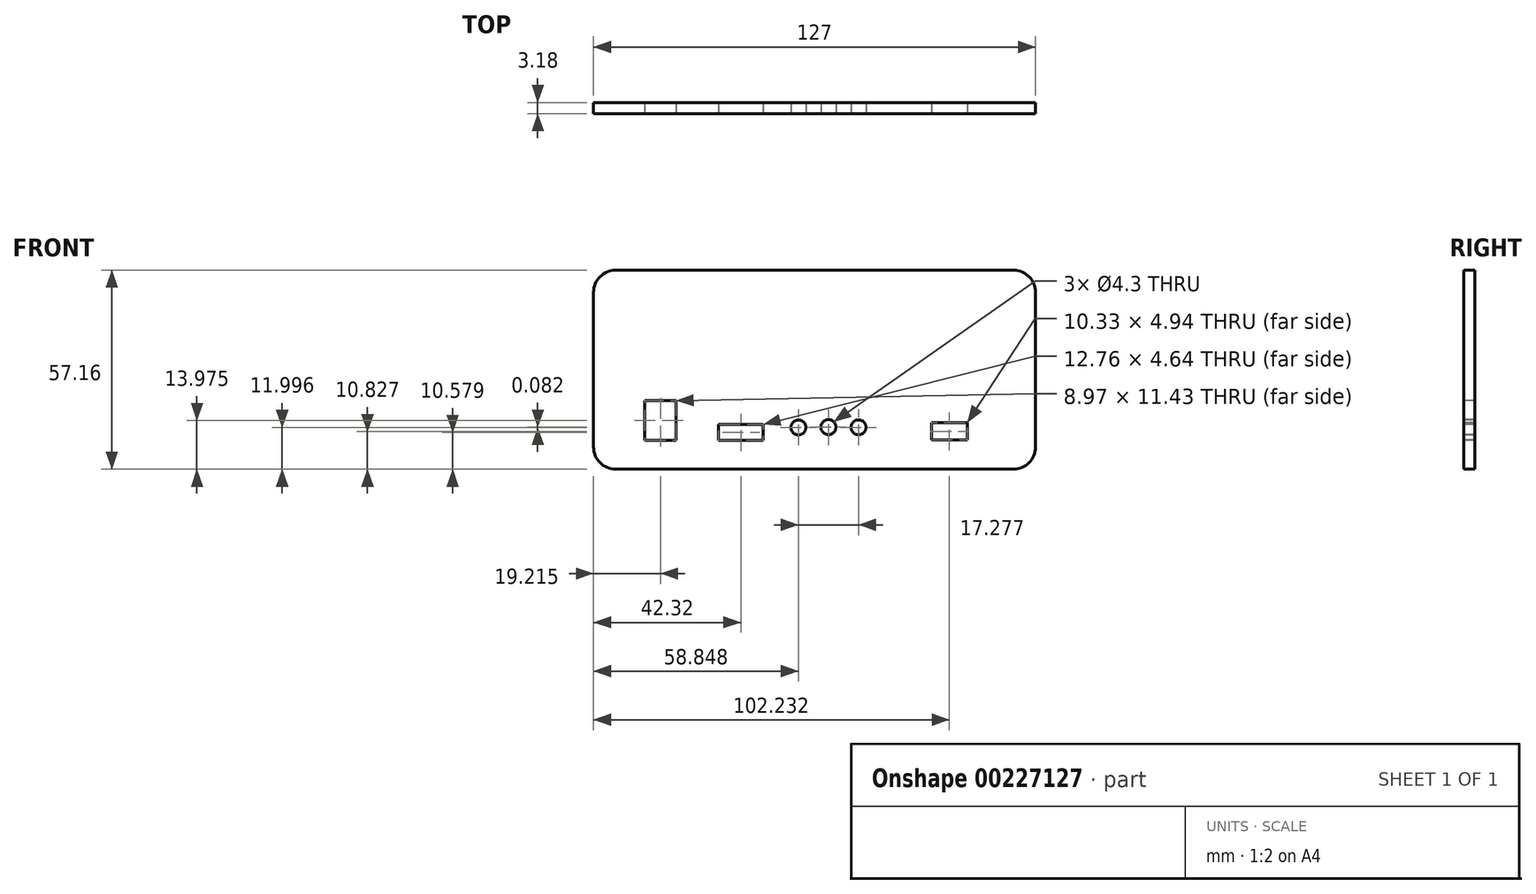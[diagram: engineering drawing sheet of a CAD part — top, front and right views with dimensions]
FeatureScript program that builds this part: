
annotation { "Feature Type Name" : "Feature", "Feature Type Description" : "" }
export const myFeature = defineFeature(function(context is Context, id is Id, definition is map)
    precondition{}
    {
        {
            var Q0;
            Q0=qCreatedBy(makeId("Front.planeOp"),FACE);
            var sketch = newSketch(context, id + "F0", { "sketchPlane" : qUnion([Q0])});
            skLineSegment(sketch, "E0.bottom", {"start": v(57.15, 28.58) * mm, "end": v(-57.15, 28.58) * mm});
            skLineSegment(sketch, "E0.top", {"start": v(57.15, -28.58) * mm, "end": v(-57.15, -28.58) * mm});
            skLineSegment(sketch, "E0.left", {"start": v(63.5, 22.22) * mm, "end": v(63.5, -22.22) * mm});
            skLineSegment(sketch, "E0.right", {"start": v(-63.5, 22.22) * mm, "end": v(-63.5, -22.22) * mm});
            skPoint(sketch, "E0.middle", {"position": v(0, 0) * mm});
            skPoint(sketch, "E1.visualSharp", {"position": v(-63.5, 28.58) * mm});
            skArc(sketch, "E1.filletArc", {"start": v(-57.15, 28.58) * mm, "mid": v(-61.64, 26.72) * mm, "end": v(-63.5, 22.22) * mm});
            skPoint(sketch, "E2.visualSharp", {"position": v(-63.5, -28.58) * mm});
            skArc(sketch, "E2.filletArc", {"start": v(-63.5, -22.22) * mm, "mid": v(-61.64, -26.72) * mm, "end": v(-57.15, -28.57) * mm});
            skPoint(sketch, "E3.visualSharp", {"position": v(63.5, -28.58) * mm});
            skArc(sketch, "E3.filletArc", {"start": v(57.15, -28.58) * mm, "mid": v(61.64, -26.72) * mm, "end": v(63.5, -22.22) * mm});
            skPoint(sketch, "E4.visualSharp", {"position": v(63.5, 28.58) * mm});
            skArc(sketch, "E4.filletArc", {"start": v(63.5, 22.22) * mm, "mid": v(61.64, 26.72) * mm, "end": v(57.15, 28.58) * mm});
            skSolve(sketch);
        }
        {
            var Q0;
            Q0=makeQuery(id+"F0.imprint","IMPRINT",FACE,{"disambiguationData":[TD([[makeQuery(id+"F0.imprint","IMPRINT",EDGE,{"derivedFrom":sQuery(id+"F0.wireOp",EDGE,"E0.bottom")}),1.0]])]});
            extrude(context, id + "F1", {"entities" : qUnion([Q0]), "depth" : 3.17 * mm, "offsetDistance" : 25.4 * mm});
        }
        {
            var Q0;
            Q0=makeQuery(id+"F1.opExtrude","CAP_FACE",FACE,{"disambiguationData":[OSD([sQuery(id+"F0.wireOp",EDGE,"E0.bottom"),sQuery(id+"F0.wireOp",EDGE,"E0.top"),sQuery(id+"F0.wireOp",EDGE,"E0.left"),sQuery(id+"F0.wireOp",EDGE,"E0.right")])],"isStart":false});
            var sketch = newSketch(context, id + "F2", { "sketchPlane" : qUnion([Q0])});
            skLineSegment(sketch, "E5.bottom", {"start": v(-60.32, 25.4) * mm, "end": v(60.33, 25.4) * mm, "construction": true});
            skLineSegment(sketch, "E5.top", {"start": v(-60.33, -25.4) * mm, "end": v(60.32, -25.4) * mm, "construction": true});
            skLineSegment(sketch, "E5.left", {"start": v(-60.32, 25.4) * mm, "end": v(-60.33, -25.4) * mm, "construction": true});
            skLineSegment(sketch, "E5.right", {"start": v(60.33, 25.4) * mm, "end": v(60.32, -25.4) * mm, "construction": true});
            skLineSegment(sketch, "E6", {"start": v(-60.33, -25.4) * mm, "end": v(-57.15, -25.4) * mm, "construction": true});
            skLineSegment(sketch, "E7", {"start": v(-57.15, -25.4) * mm, "end": v(-48.77, -25.4) * mm, "construction": true});
            skLineSegment(sketch, "E8", {"start": v(0, -25.4) * mm, "end": v(0, -20.32) * mm, "construction": true});
            skLineSegment(sketch, "E9", {"start": v(0, -20.32) * mm, "end": v(-60.33, -20.32) * mm, "construction": true});
            skLineSegment(sketch, "E10.bottom", {"start": v(-48.77, -20.32) * mm, "end": v(-39.8, -20.32) * mm});
            skLineSegment(sketch, "E10.top", {"start": v(-48.77, -8.9) * mm, "end": v(-39.8, -8.9) * mm});
            skLineSegment(sketch, "E10.left", {"start": v(-48.77, -20.32) * mm, "end": v(-48.77, -8.9) * mm});
            skLineSegment(sketch, "E10.right", {"start": v(-39.8, -20.32) * mm, "end": v(-39.8, -8.9) * mm});
            skLineSegment(sketch, "E11.bottom", {"start": v(-27.56, -20.32) * mm, "end": v(-14.8, -20.32) * mm});
            skLineSegment(sketch, "E11.top", {"start": v(-27.56, -15.68) * mm, "end": v(-14.8, -15.68) * mm});
            skLineSegment(sketch, "E11.left", {"start": v(-27.56, -20.32) * mm, "end": v(-27.56, -15.68) * mm});
            skLineSegment(sketch, "E11.right", {"start": v(-14.8, -20.32) * mm, "end": v(-14.8, -15.68) * mm});
            skCircle(sketch, "E12", {"center": v(-4.65, -16.58) * mm, "radius": 2.15 * mm});
            skCircle(sketch, "E13", {"center": v(3.97, -16.5) * mm, "radius": 2.15 * mm});
            skCircle(sketch, "E14", {"center": v(12.62, -16.56) * mm, "radius": 2.15 * mm});
            skLineSegment(sketch, "E15.bottom", {"start": v(33.56, -15.28) * mm, "end": v(43.9, -15.28) * mm});
            skLineSegment(sketch, "E15.top", {"start": v(33.56, -20.22) * mm, "end": v(43.9, -20.22) * mm});
            skLineSegment(sketch, "E15.left", {"start": v(33.56, -15.28) * mm, "end": v(33.56, -20.22) * mm});
            skLineSegment(sketch, "E15.right", {"start": v(43.9, -15.28) * mm, "end": v(43.9, -20.22) * mm});
            skSolve(sketch);
        }
        {
            var Q0;
            Q0=makeQuery(id+"F2.imprint","IMPRINT",FACE,{"disambiguationData":[TD([[makeQuery(id+"F2.imprint","IMPRINT",EDGE,{"derivedFrom":sQuery(id+"F2.wireOp",EDGE,"E10.bottom")}),1.0]])]});
            var Q1;
            Q1=makeQuery(id+"F2.imprint","IMPRINT",FACE,{"disambiguationData":[TD([[makeQuery(id+"F2.imprint","IMPRINT",EDGE,{"derivedFrom":sQuery(id+"F2.wireOp",EDGE,"E11.bottom")}),1.0]])]});
            var Q2;
            Q2=makeQuery(id+"F2.imprint","IMPRINT",FACE,{"disambiguationData":[TD([[makeQuery(id+"F2.imprint","IMPRINT",EDGE,{"derivedFrom":sQuery(id+"F2.wireOp",EDGE,"E12")}),1.0]])]});
            var Q3;
            Q3=makeQuery(id+"F2.imprint","IMPRINT",FACE,{"disambiguationData":[TD([[makeQuery(id+"F2.imprint","IMPRINT",EDGE,{"derivedFrom":sQuery(id+"F2.wireOp",EDGE,"E13")}),1.0]])]});
            var Q4;
            Q4=makeQuery(id+"F2.imprint","IMPRINT",FACE,{"disambiguationData":[TD([[makeQuery(id+"F2.imprint","IMPRINT",EDGE,{"derivedFrom":sQuery(id+"F2.wireOp",EDGE,"E14")}),1.0]])]});
            var Q5;
            Q5=makeQuery(id+"F2.imprint","IMPRINT",FACE,{"disambiguationData":[TD([[makeQuery(id+"F2.imprint","IMPRINT",EDGE,{"derivedFrom":sQuery(id+"F2.wireOp",EDGE,"E15.bottom")}),-1.0]])]});
            extrude(context, id + "F3", {"entities" : qUnion([Q0, Q1, Q2, Q3, Q4, Q5]), "operationType" : NewBodyOperationType.REMOVE, "oppositeDirection" : true, "depth" : 25.4 * mm, "offsetDistance" : 25.4 * mm});
        }
    });
